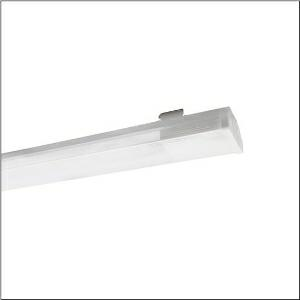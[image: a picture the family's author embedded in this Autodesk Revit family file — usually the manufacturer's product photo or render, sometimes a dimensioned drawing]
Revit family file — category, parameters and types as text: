
# Revit family: modario_r__31_gen_2_53bm812du4hxd2_4cd4
name_source: partatom
category: Lighting Fixtures
units: mm (PartAtom-declared; Revit-internal decimal feet)

## family parameters
Cut with Voids When Loaded = No
Host = Face
Light Source = No
Part Type = Normal
Room Calculation Point = No
Round Connector Dimension = Use Diameter
Shared = No

## types (1)
- --- (1 x LED, 17250 lm, 92.2 W, 4000K)
    Apparent Load = 92 VA
    CIE Flux Codes = 47 80 95 93 100
    Color Rendering = 80
    Color Temperature = 4000K
    Default Elevation = 1800 mm
    Description = Modario® 31 Gen.2, luminaire insert, of sheet steel, coil coated, white, length: 2.392mm, width: 81mm, height: 82mm, 8x system unit, system units: 299mm, LED rated luminous flux: 17.250lm, light colour: 840, control gear: DALI 2, control gear: ECG DALI, with plug, 5-pole, with phase selection, mains connection: 220..240V, AC, 50/60Hz, rated input power: 92W, through-wiring accessed according to module size, primary optical cover: cover, of PMMA, light emission: direct distribution, primary light characteristic: symmetric, protection rating (complete): IP20, protection rating (LED compartment): IP50, insulation class (complete): insulation class I (protective earthing), certification: CE, ENEC, VDE, UKCA, impact resistance: IK03, permissible ambient temperature for indoor applications: -25..+35°C, corresponds to IFS (International Featured Standards) requirements for safety and quality in the food industry, reducing of maximum allowable ambient temperature of 5°C with ceiling mounting, packaging unit: 1 piece
    Height = 92 mm
    Lamp = 1 x LED
    Lamp Light Flux = 17250 lm
    Lamp Power = 92.2 W
    Lamp count = 1
    Length = 2392 mm
    Luminous efficacy = 187 lm/W
    Manufacturer = Siteco
    ModVariant = No
    Model = 53BM812DU4HXD2
    Mounting Place = Ceiling
    Mounting Type = Pendant
    Number of Poles = 1
    OnlyDefault = Yes
    Power Factor = 1
    Product Name = Modario® 31 Gen.2
    Product group = luminaire insert
    ProductGroupID = 902
    Protection Class = Protection class I
    Protection Degree = IP 20
    RLX_Detail_Level = 1
    RLX_Emergency_Light_Flux = 0 lm
    RLX_Emergency_Type = 0
    RLX_Emergency_Type_DB = No
    RlxData = <blob elided: 37977 chars, md5=ed89d969>
    Socket = socket
    Standby Power = 0 W
    System Light Flux = 17250 lm
    System Power = 92 W
    Type Comments = factory setting: luminous flux: 100 % | dim-lin: 254 | 425 mA
    Type Image = l_1341883.jpg
    URL = http://relux.com
    VarID = @adj_043508
    Voltage = 0 V
    Weight = 0.00 kg
    Width = 81 mm

## geometry (parser evidence)
native form markers: Blend x4, Sweep x12
no freeform markers — native parametric forms only
